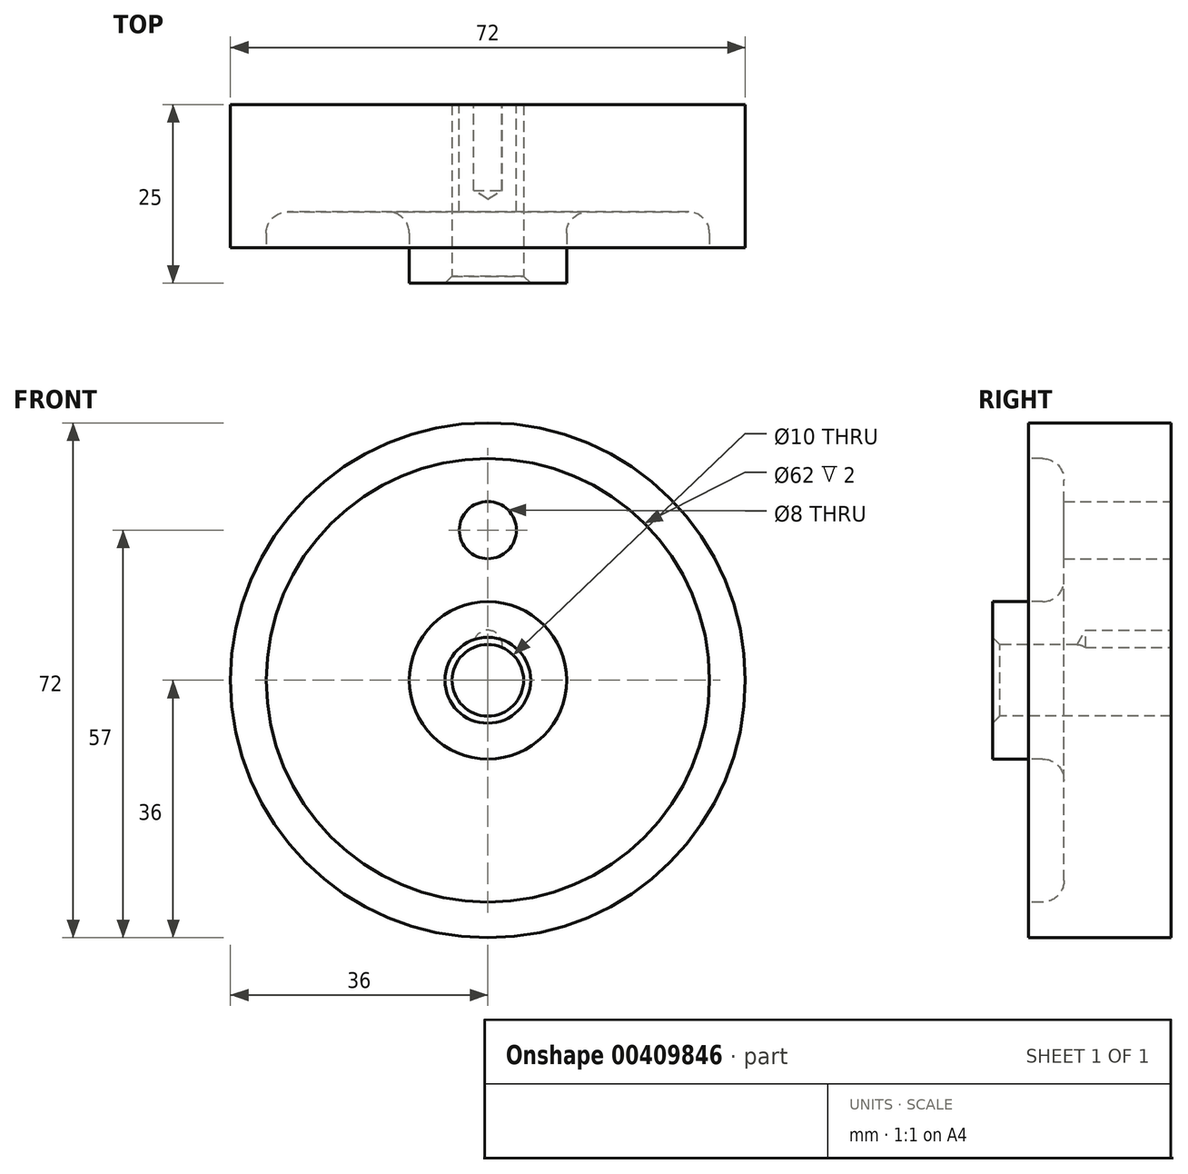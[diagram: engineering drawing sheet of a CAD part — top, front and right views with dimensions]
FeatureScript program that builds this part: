
annotation { "Feature Type Name" : "Feature", "Feature Type Description" : "" }
export const myFeature = defineFeature(function(context is Context, id is Id, definition is map)
    precondition{}
    {
        {
            var Q0;
            Q0=qCreatedBy(makeId("Right.planeOp"),FACE);
            var sketch = newSketch(context, id + "F0", { "sketchPlane" : qUnion([Q0])});
            skLineSegment(sketch, "E0", {"start": v(-12, 0) * mm, "end": v(30.06, 0) * mm, "construction": true});
            skLineSegment(sketch, "E1", {"start": v(0, 5) * mm, "end": v(0, 11) * mm});
            skLineSegment(sketch, "E2", {"start": v(0, 11) * mm, "end": v(7, 11) * mm});
            skLineSegment(sketch, "E3", {"start": v(10, 14) * mm, "end": v(10, 28) * mm});
            skLineSegment(sketch, "E4", {"start": v(7, 31) * mm, "end": v(5, 31) * mm});
            skLineSegment(sketch, "E5", {"start": v(5, 31) * mm, "end": v(5, 36) * mm});
            skLineSegment(sketch, "E6", {"start": v(5, 36) * mm, "end": v(25, 36) * mm});
            skLineSegment(sketch, "E7", {"start": v(25, 36) * mm, "end": v(25, 5) * mm});
            skLineSegment(sketch, "E8", {"start": v(25, 5) * mm, "end": v(0, 5) * mm});
            skPoint(sketch, "E9.visualSharp", {"position": v(10, 31) * mm});
            skArc(sketch, "E9.filletArc", {"start": v(10, 28) * mm, "mid": v(9.12, 30.12) * mm, "end": v(7, 31) * mm});
            skPoint(sketch, "E10.visualSharp", {"position": v(10, 11) * mm});
            skArc(sketch, "E10.filletArc", {"start": v(7, 11) * mm, "mid": v(9.12, 11.88) * mm, "end": v(10, 14) * mm});
            skSolve(sketch);
        }
        {
            var Q0;
            Q0 = qSketchRegion(id + "F0", true);
            var Q1;
            Q1=sQuery(id+"F0.wireOp",EDGE,"E0");
            revolve(context, id + "F1", {"entities" : qUnion([Q0]), "axis" : qUnion([Q1]), "revolveType" : RevolveType.FULL});
        }
        {
            var Q0;
            Q0=makeQuery(id+"F1.opRevolve","SWEPT_EDGE",EDGE,{"disambiguationData":[OSD([sQuery(id+"F0.wireOp",EDGE,"E1"),sQuery(id+"F0.wireOp",EDGE,"E8")])]});
            chamfer(context, id + "F2", {"entities" : qUnion([Q0]), "width" : 1 * mm, "tangentPropagation" : true});
        }
        {
            var Q0;
            Q0=makeQuery(id+"F1.opRevolve","SWEPT_FACE",FACE,{"disambiguationData":[OSD([sQuery(id+"F0.wireOp",EDGE,"E7")])]});
            var sketch = newSketch(context, id + "F3", { "sketchPlane" : qUnion([Q0])});
            skCircle(sketch, "E11", {"center": v(0, 21) * mm, "radius": 4 * mm});
            skSolve(sketch);
        }
        {
            var Q0;
            Q0 = qSketchRegion(id + "F3", true);
            extrude(context, id + "F4", {"entities" : qUnion([Q0]), "operationType" : NewBodyOperationType.REMOVE, "endBound" : BoundingType.UP_TO_NEXT, "oppositeDirection" : true, "depth" : 25 * mm});
        }
        {
            var Q0;
            Q0=makeQuery(id+"F1.opRevolve","SWEPT_FACE",FACE,{"disambiguationData":[OSD([sQuery(id+"F0.wireOp",EDGE,"E7")])]});
            var sketch = newSketch(context, id + "F5", { "sketchPlane" : qUnion([Q0])});
            skCircle(sketch, "E12.0", {"center": v(0, 0) * mm, "radius": 5 * mm});
            skPoint(sketch, "E13", {"position": v(0, 5) * mm});
            skSolve(sketch);
        }
        {
            var Q0;
            Q0=sQuery(id+"F5.wireOp",VERTEX,"E13");
            var Q1;
            Q1=makeQuery(id+"F1.opRevolve","SWEPT_BODY",BODY,{"disambiguationData":[OSD([sQuery(id+"F0.wireOp",EDGE,"E1"),sQuery(id+"F0.wireOp",EDGE,"E2"),sQuery(id+"F0.wireOp",EDGE,"E3"),sQuery(id+"F0.wireOp",EDGE,"E4"),sQuery(id+"F0.wireOp",EDGE,"E5"),sQuery(id+"F0.wireOp",EDGE,"E6"),sQuery(id+"F0.wireOp",EDGE,"E7"),sQuery(id+"F0.wireOp",EDGE,"E8"),sQuery(id+"F0.wireOp",EDGE,"E9.filletArc"),sQuery(id+"F0.wireOp",EDGE,"E10.filletArc")])]});
            hole(context, id + "F6", {"style" : HoleStyle.SIMPLE, "endStyle" : HoleEndStyle.BLIND, "standardTappedOrClearance" : lookupTablePath({ "standard" : "ISO", "size" : "4", "type" : "Drilled" }), "standardBlindInLast" : lookupTablePath({ "standard" : "ISO", "size" : "4", "type" : "Drilled" }), "holeDiameter" : 4 * mm, "holeDepth" : 12 * mm, "isTappedThrough" : true, "tappedDepth" : 12 * mm, "tapClearance" : 3, "startFromSketch" : true, "locations" : qUnion([Q0]), "scope" : qUnion([Q1])});
        }
    });
